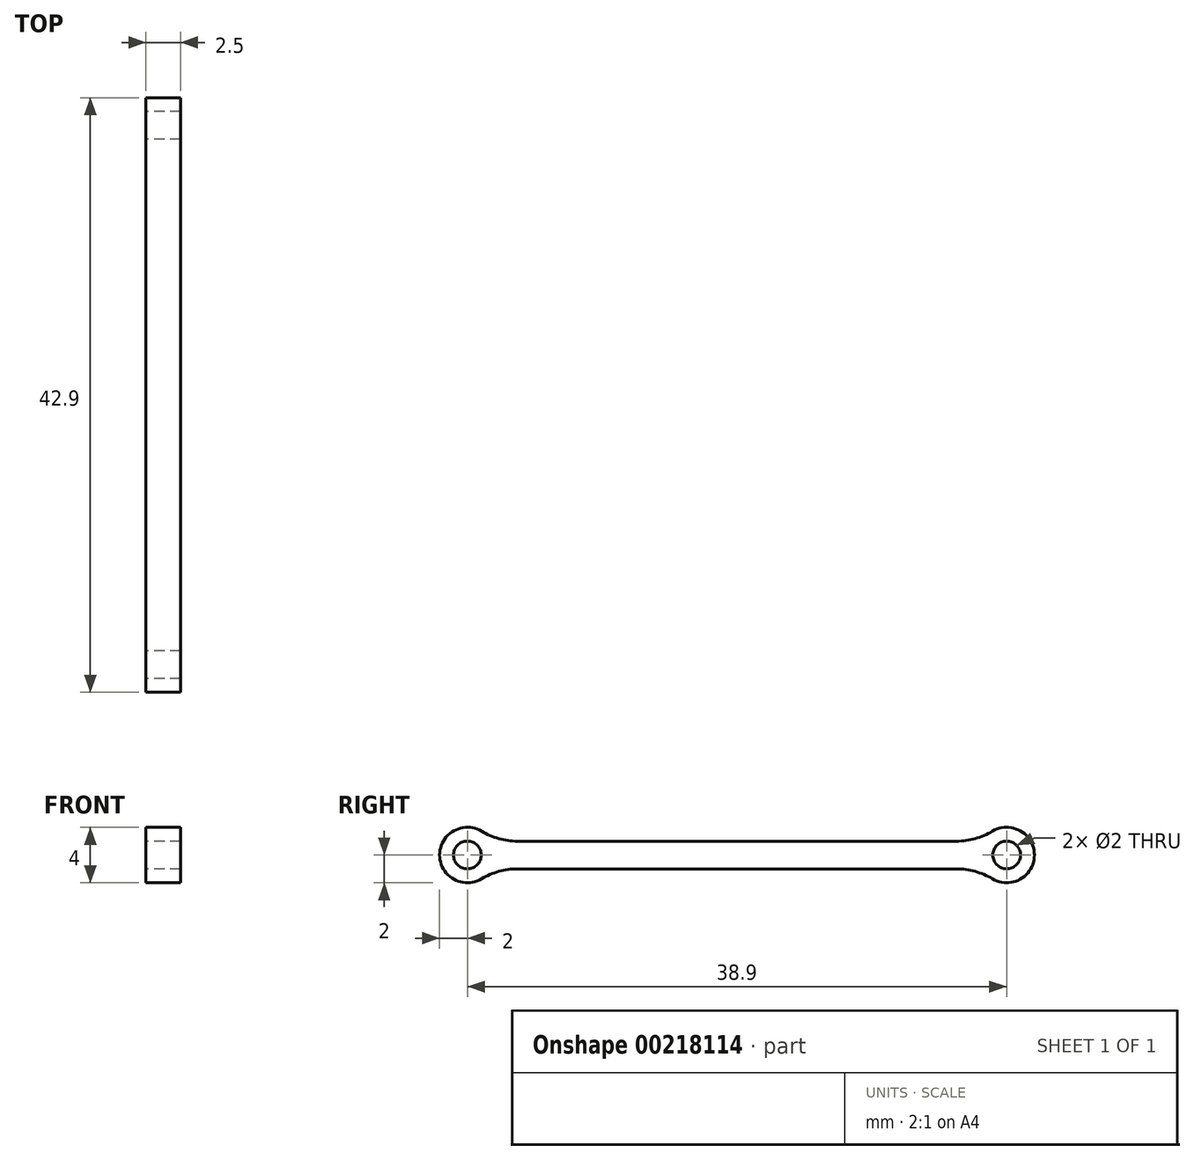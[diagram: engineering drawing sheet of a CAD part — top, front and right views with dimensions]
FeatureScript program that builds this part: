
annotation { "Feature Type Name" : "Feature", "Feature Type Description" : "" }
export const myFeature = defineFeature(function(context is Context, id is Id, definition is map)
    precondition{}
    {
        {
            var Q0;
            Q0=qCreatedBy(makeId("Right.planeOp"),FACE);
            var sketch = newSketch(context, id + "F0", { "sketchPlane" : qUnion([Q0])});
            skLineSegment(sketch, "E0.bottom", {"start": v(15.84, -1) * mm, "end": v(-15.84, -1) * mm});
            skLineSegment(sketch, "E0.top", {"start": v(15.84, 1) * mm, "end": v(-15.84, 1) * mm});
            skPoint(sketch, "E0.middle", {"position": v(0, 0) * mm});
            skCircle(sketch, "E1", {"center": v(-19.45, 0) * mm, "radius": 1 * mm});
            skCircle(sketch, "E2", {"center": v(19.45, 0) * mm, "radius": 1 * mm});
            skArc(sketch, "E3", {"start": v(18.42, -1.71) * mm, "mid": v(21.45, 0) * mm, "end": v(18.42, 1.71) * mm});
            skArc(sketch, "E4", {"start": v(-18.42, 1.71) * mm, "mid": v(-21.45, 0) * mm, "end": v(-18.42, -1.71) * mm});
            skPoint(sketch, "E5.orphan", {"position": v(-19.45, -1) * mm});
            skPoint(sketch, "E6.orphan", {"position": v(-19.45, 1) * mm});
            skPoint(sketch, "E7.orphan", {"position": v(19.45, 1) * mm});
            skPoint(sketch, "E8.orphan", {"position": v(19.45, -1) * mm});
            skPoint(sketch, "E9.visualSharp", {"position": v(17.72, 1) * mm});
            skArc(sketch, "E9.filletArc", {"start": v(15.84, 1) * mm, "mid": v(17.18, 1.18) * mm, "end": v(18.42, 1.71) * mm});
            skPoint(sketch, "E10.visualSharp", {"position": v(17.72, -1) * mm});
            skArc(sketch, "E10.filletArc", {"start": v(18.42, -1.71) * mm, "mid": v(17.18, -1.18) * mm, "end": v(15.84, -1) * mm});
            skPoint(sketch, "E11.visualSharp", {"position": v(-17.72, -1) * mm});
            skArc(sketch, "E11.filletArc", {"start": v(-15.84, -1) * mm, "mid": v(-17.18, -1.18) * mm, "end": v(-18.42, -1.71) * mm});
            skPoint(sketch, "E12.visualSharp", {"position": v(-17.72, 1) * mm});
            skArc(sketch, "E12.filletArc", {"start": v(-18.42, 1.71) * mm, "mid": v(-17.18, 1.18) * mm, "end": v(-15.84, 1) * mm});
            skSolve(sketch);
        }
        {
            var Q0;
            Q0=makeQuery(id+"F0.imprint","IMPRINT",FACE,{"disambiguationData":[TD([[makeQuery(id+"F0.imprint","IMPRINT",EDGE,{"derivedFrom":sQuery(id+"F0.wireOp",EDGE,"E0.bottom")}),-1.0]])]});
            extrude(context, id + "F1", {"entities" : qUnion([Q0]), "depth" : 2.5 * mm});
        }
    });
